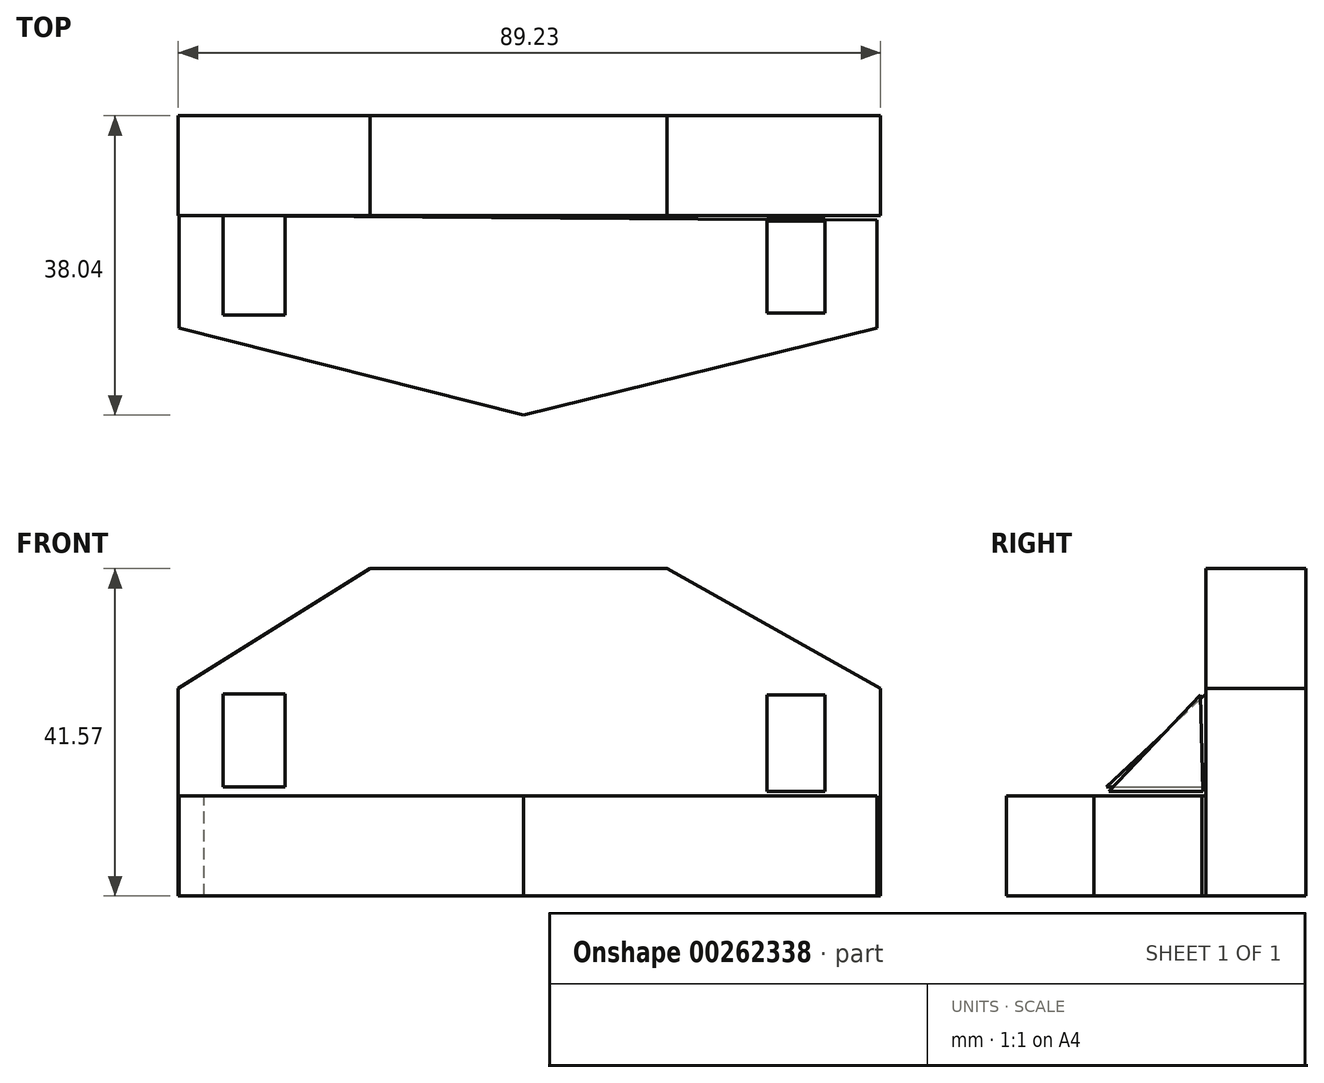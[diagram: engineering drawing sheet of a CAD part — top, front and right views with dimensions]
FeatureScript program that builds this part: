
annotation { "Feature Type Name" : "Feature", "Feature Type Description" : "" }
export const myFeature = defineFeature(function(context is Context, id is Id, definition is map)
    precondition{}
    {
        {
            var Q0;
            Q0=qCreatedBy(makeId("Front.planeOp"),FACE);
            var sketch = newSketch(context, id + "F0", { "sketchPlane" : qUnion([Q0])});
            skLineSegment(sketch, "E0", {"start": v(-25, 41.57) * mm, "end": v(-49.4, 26.33) * mm});
            skLineSegment(sketch, "E1", {"start": v(-25, 41.57) * mm, "end": v(12.68, 41.57) * mm});
            skLineSegment(sketch, "E2", {"start": v(12.68, 41.57) * mm, "end": v(39.84, 26.33) * mm});
            skLineSegment(sketch, "E3", {"start": v(39.84, 26.33) * mm, "end": v(39.84, 0) * mm});
            skLineSegment(sketch, "E4", {"start": v(-49.4, 26.33) * mm, "end": v(-49.4, 0) * mm});
            skLineSegment(sketch, "E5", {"start": v(-49.4, 0) * mm, "end": v(39.84, 0) * mm});
            skSolve(sketch);
        }
        {
            var Q0;
            Q0=makeQuery(id+"F0.imprint","IMPRINT",FACE,{"disambiguationData":[TD([[makeQuery(id+"F0.imprint","IMPRINT",EDGE,{"derivedFrom":sQuery(id+"F0.wireOp",EDGE,"E0")}),1.0]])]});
            extrude(context, id + "F1", {"entities" : qUnion([Q0]), "depth" : 12.7 * mm});
        }
        {
            var Q0;
            Q0=qCreatedBy(makeId("Top.planeOp"),FACE);
            var sketch = newSketch(context, id + "F2", { "sketchPlane" : qUnion([Q0])});
            skLineSegment(sketch, "E6", {"start": v(-49.26, -12.68) * mm, "end": v(-49.26, -26.96) * mm});
            skLineSegment(sketch, "E7", {"start": v(39.35, -13.26) * mm, "end": v(39.35, -26.96) * mm});
            skLineSegment(sketch, "E8", {"start": v(39.35, -26.96) * mm, "end": v(-5.54, -38.04) * mm});
            skLineSegment(sketch, "E9", {"start": v(-5.54, -38.04) * mm, "end": v(-49.26, -26.96) * mm});
            skLineSegment(sketch, "E10", {"start": v(-49.26, -12.68) * mm, "end": v(39.35, -13.26) * mm});
            skSolve(sketch);
        }
        {
            var Q0;
            Q0=makeQuery(id+"F2.imprint","IMPRINT",FACE,{"disambiguationData":[TD([[makeQuery(id+"F2.imprint","IMPRINT",EDGE,{"derivedFrom":sQuery(id+"F2.wireOp",EDGE,"E6")}),1.0]])]});
            extrude(context, id + "F3", {"entities" : qUnion([Q0]), "operationType" : NewBodyOperationType.ADD, "depth" : 12.7 * mm});
        }
        {
            var Q0;
            Q0=qCreatedBy(makeId("Right.planeOp"),FACE);
            var sketch = newSketch(context, id + "F4", { "sketchPlane" : qUnion([Q0])});
            skLineSegment(sketch, "E11", {"start": v(-13.12, 13.26) * mm, "end": v(-25.07, 13.26) * mm});
            skLineSegment(sketch, "E12", {"start": v(-25.07, 13.26) * mm, "end": v(-13.4, 25.5) * mm});
            skLineSegment(sketch, "E13", {"start": v(-13.4, 25.5) * mm, "end": v(-13.12, 13.26) * mm});
            skSolve(sketch);
        }
        {
            var Q0;
            Q0 = qSketchRegion(id + "F4", true);
            extrude(context, id + "F5", {"entities" : qUnion([Q0]), "depth" : 32.77 * mm});
        }
        {
            var Q0;
            Q0=makeQuery(id+"F5.opExtrude","CAP_FACE",FACE,{"disambiguationData":[OSD([sQuery(id+"F4.wireOp",EDGE,"E11"),sQuery(id+"F4.wireOp",EDGE,"E12"),sQuery(id+"F4.wireOp",EDGE,"E13")])],"isStart":true});
            extrude(context, id + "F6", {"entities" : qUnion([Q0]), "operationType" : NewBodyOperationType.REMOVE, "oppositeDirection" : true, "depth" : 25.4 * mm});
        }
        {
            var Q0;
            Q0=qCreatedBy(makeId("Right.planeOp"),FACE);
            var sketch = newSketch(context, id + "F7", { "sketchPlane" : qUnion([Q0])});
            skLineSegment(sketch, "E14", {"start": v(-25.36, 13.85) * mm, "end": v(-12.53, 13.85) * mm});
            skLineSegment(sketch, "E15", {"start": v(-12.53, 13.85) * mm, "end": v(-12.53, 25.8) * mm});
            skLineSegment(sketch, "E16", {"start": v(-12.53, 25.8) * mm, "end": v(-25.36, 13.85) * mm});
            skSolve(sketch);
        }
        {
            var Q0;
            Q0 = qSketchRegion(id + "F7", true);
            extrude(context, id + "F8", {"entities" : qUnion([Q0]), "operationType" : NewBodyOperationType.ADD, "oppositeDirection" : true, "depth" : 43.69 * mm});
        }
        {
            var Q0;
            Q0=makeQuery(id+"F8.opExtrude","CAP_FACE",FACE,{"disambiguationData":[OSD([sQuery(id+"F7.wireOp",EDGE,"E14"),sQuery(id+"F7.wireOp",EDGE,"E15"),sQuery(id+"F7.wireOp",EDGE,"E16")])],"isStart":true});
            extrude(context, id + "F9", {"entities" : qUnion([Q0]), "operationType" : NewBodyOperationType.REMOVE, "oppositeDirection" : true, "depth" : 35.81 * mm});
        }
    });
